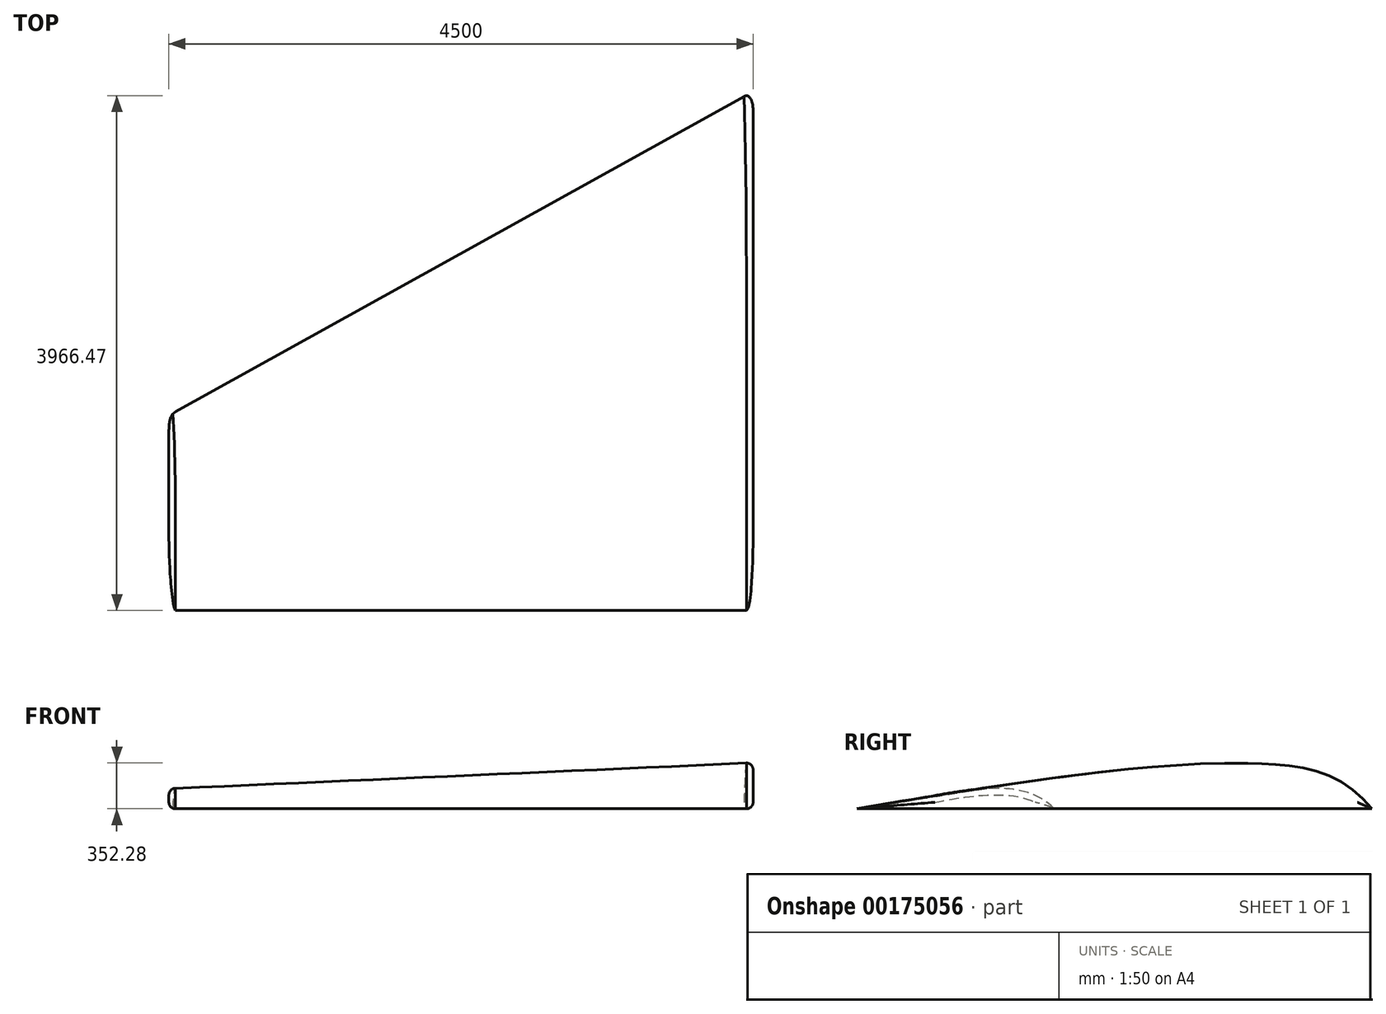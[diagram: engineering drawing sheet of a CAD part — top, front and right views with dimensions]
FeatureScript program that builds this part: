
annotation { "Feature Type Name" : "Feature", "Feature Type Description" : "" }
export const myFeature = defineFeature(function(context is Context, id is Id, definition is map)
    precondition{}
    {
        {
            var Q0;
            Q0=qCreatedBy(makeId("Right.planeOp"),FACE);
            var sketch = newSketch(context, id + "F0", { "sketchPlane" : qUnion([Q0])});
            skLineSegment(sketch, "E0", {"start": v(-2000, 0) * mm, "end": v(2000, 0) * mm});
            skFitSpline(sketch, "E1", {"points": [v(2000, 0) * mm, v(1150, 350) * mm, v(-2000, 0) * mm], "startDerivative": vector(-1838.86, 2296.85) * mm, "endDerivative": vector(-6608.78, -1143.42) * mm});
            skSolve(sketch);
        }
        {
            var Q0;
            Q0=qCreatedBy(makeId("Right.planeOp"),FACE);
            cPlane(context, id + "F1", {"entities" : qUnion([Q0]), "cplaneType" : CPlaneType.OFFSET, "offset" : 4500 * mm, "oppositeDirection" : true, "width" : 150 * mm, "height" : 150 * mm});
        }
        {
            var Q0;
            Q0=qCreatedBy(id+"F1.planeOp",FACE);
            var sketch = newSketch(context, id + "F2", { "sketchPlane" : qUnion([Q0])});
            skFitSpline(sketch, "E2", {"points": [v(-497.75, 0) * mm, v(-1997.75, 0) * mm], "startDerivative": vector(-949.58, 971.46) * mm, "endDerivative": vector(-1587.82, -146.42) * mm});
            skLineSegment(sketch, "E3", {"start": v(-497.75, 0) * mm, "end": v(-1997.75, 0) * mm});
            skSolve(sketch);
        }
        {
            var Q0;
            Q0=makeQuery(id+"F0.imprint","IMPRINT",FACE,{"disambiguationData":[TD([[makeQuery(id+"F0.imprint","IMPRINT",EDGE,{"derivedFrom":sQuery(id+"F0.wireOp",EDGE,"E0")}),1.0]])]});
            var Q1;
            Q1=makeQuery(id+"F2.imprint","IMPRINT",FACE,{"disambiguationData":[TD([[makeQuery(id+"F2.imprint","IMPRINT",EDGE,{"derivedFrom":sQuery(id+"F2.wireOp",EDGE,"E2")}),1.0]])]});
            loft(context, id + "F3", {"sheetProfilesArray" : [{ "sheetProfileEntities" : qUnion([Q0]) }, { "sheetProfileEntities" : qUnion([Q1]) }]});
        }
        {
            var Q0;
            Q0=makeQuery(id+"F3.opLoft","CAP_FACE",FACE,{"disambiguationData":[OSD([makeQuery(id+"F0.imprint","IMPRINT",FACE,{"disambiguationData":[TD([[makeQuery(id+"F0.imprint","IMPRINT",EDGE,{"derivedFrom":sQuery(id+"F0.wireOp",EDGE,"E0")}),1.0]])]})])],"isStart":true});
            var Q1;
            Q1=makeQuery(id+"F3.opLoft","CAP_FACE",FACE,{"disambiguationData":[OSD([makeQuery(id+"F2.imprint","IMPRINT",FACE,{"disambiguationData":[TD([[makeQuery(id+"F2.imprint","IMPRINT",EDGE,{"derivedFrom":sQuery(id+"F2.wireOp",EDGE,"E2")}),1.0]])]})])],"isStart":true});
            fillet(context, id + "F4", {"entities" : qUnion([Q0, Q1]), "radius" : 50 * mm, "tangentPropagation" : true, "allowEdgeOverflow" : false});
        }
    });
